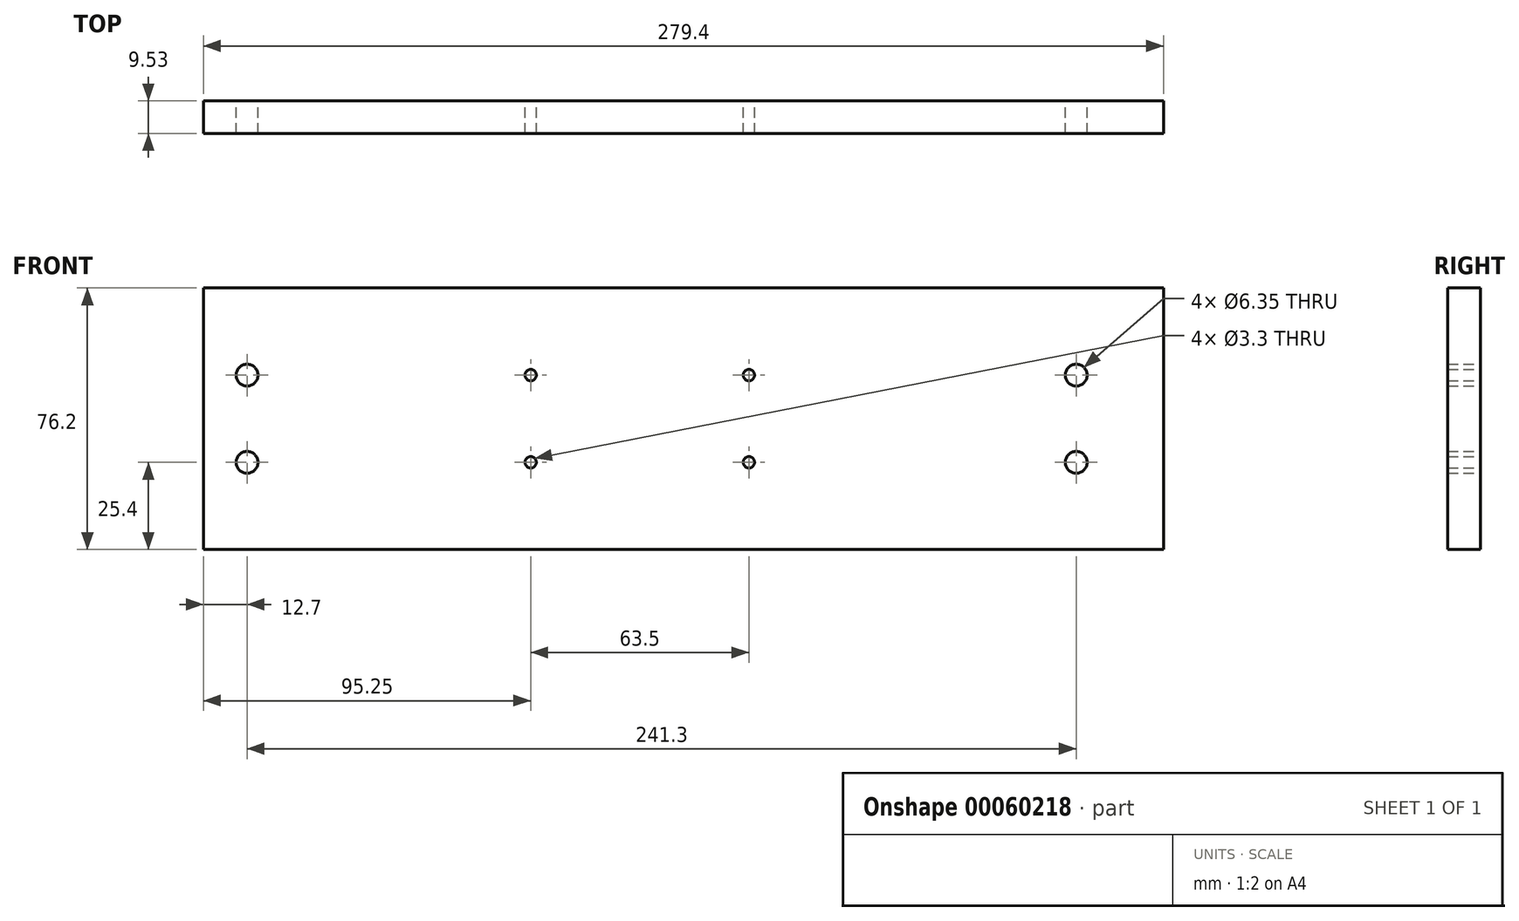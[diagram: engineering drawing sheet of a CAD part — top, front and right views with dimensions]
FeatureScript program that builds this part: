
annotation { "Feature Type Name" : "Feature", "Feature Type Description" : "" }
export const myFeature = defineFeature(function(context is Context, id is Id, definition is map)
    precondition{}
    {
        {
            var Q0;
            Q0=qCreatedBy(makeId("Front.planeOp"),FACE);
            var sketch = newSketch(context, id + "F0", { "sketchPlane" : qUnion([Q0])});
            skLineSegment(sketch, "E0.rect.bottom", {"start": v(139.7, -38.1) * mm, "end": v(-139.7, -38.1) * mm});
            skLineSegment(sketch, "E0.rect.top", {"start": v(139.7, 38.1) * mm, "end": v(-139.7, 38.1) * mm});
            skLineSegment(sketch, "E0.rect.left", {"start": v(139.7, -38.1) * mm, "end": v(139.7, 38.1) * mm});
            skLineSegment(sketch, "E0.rect.right", {"start": v(-139.7, -38.1) * mm, "end": v(-139.7, 38.1) * mm});
            skPoint(sketch, "E0.rect.middle", {"position": v(0, 0) * mm});
            skCircle(sketch, "E1", {"center": v(-127, 12.7) * mm, "radius": 3.18 * mm});
            skCircle(sketch, "E2", {"center": v(-44.45, 12.7) * mm, "radius": 1.65 * mm});
            skCircle(sketch, "E3", {"center": v(19.05, 12.7) * mm, "radius": 1.65 * mm});
            skCircle(sketch, "E4", {"center": v(114.3, 12.7) * mm, "radius": 3.18 * mm});
            skCircle(sketch, "E5.MirrorC", {"center": v(114.3, -12.7) * mm, "radius": 3.18 * mm});
            skCircle(sketch, "E6.MirrorC", {"center": v(19.05, -12.7) * mm, "radius": 1.65 * mm});
            skCircle(sketch, "E7.MirrorC", {"center": v(-44.45, -12.7) * mm, "radius": 1.65 * mm});
            skCircle(sketch, "E8.MirrorC", {"center": v(-127, -12.7) * mm, "radius": 3.18 * mm});
            skSolve(sketch);
        }
        {
            var Q0;
            Q0 = qSketchRegion(id + "F0", true);
            extrude(context, id + "F1", {"entities" : qUnion([Q0]), "depth" : 9.52 * mm});
        }
    });
